# Revit family: Worksurfaces-Teknion-JNWFG_Writable_Glass_Center_Beam_Mounted-R2018
name_source: partatom
category: Furniture
revit_build: Autodesk Revit 2018 (Build: 20190510_1515(x64)
units: mm (PartAtom-declared; Revit-internal decimal feet)

## family parameters
Always vertical = Yes
Cut with Voids When Loaded = No
OmniClass Number = 23.40.20.00
OmniClass Title = General Furniture and Specialties
Room Calculation Point = No
Shared = Yes
Work Plane-Based = No

## types (1)
- 38" Depth
    Assembly Code = E2020200
    Companion Finish = Paint - Teknion - Accent - Mineral Teal
    Description = Writable Glass Worksurface – Center Beam-Mounted, 38" Depth, With Companion Marker Kit
    Manufacturer = Teknion
    Manufacturer Fax = 416.661.4586
    Model = JNWFG38__K
    Part Number = JNWFG
    Product Documentation Link = https://www.teknion.com
    Product Line = Expansion Cityline
    Product Page URL = https://www.teknion.com
    Series = Expansion Cityline
    Sustainability Data = https://www.teknion.com
    URL = www.teknion.com
    Unit Weight URL = http://www.teknion.com
    Warranty = http://www.teknion.com

## geometry (parser evidence)
native form markers: Sweep x2
no freeform markers — native parametric forms only
